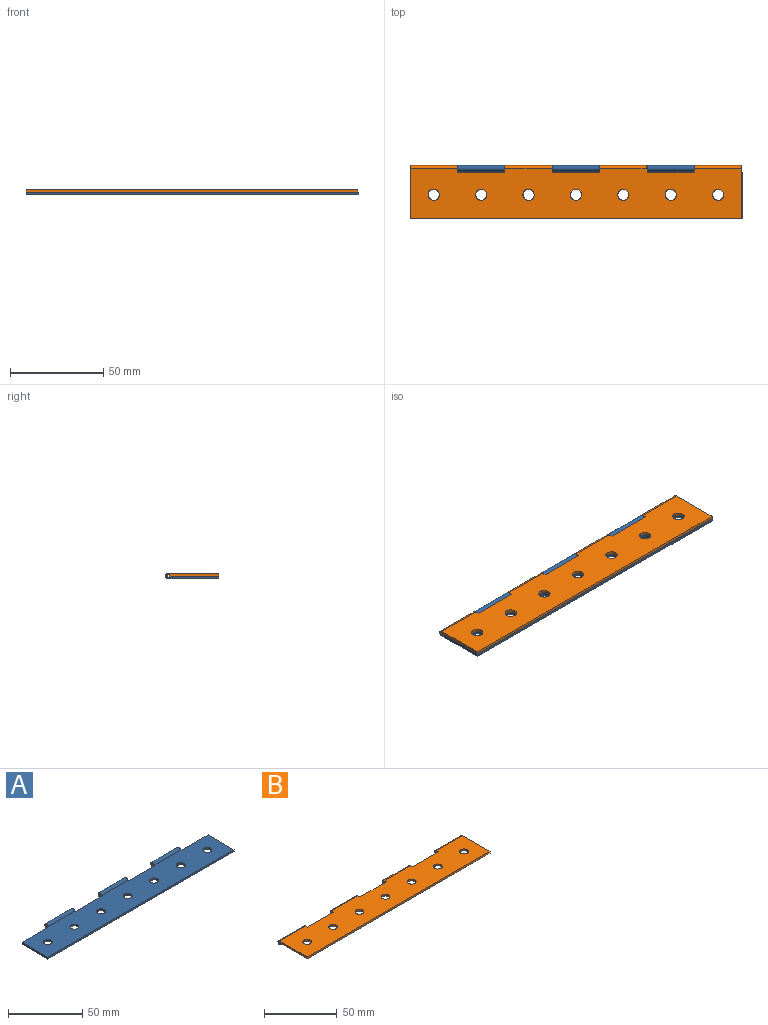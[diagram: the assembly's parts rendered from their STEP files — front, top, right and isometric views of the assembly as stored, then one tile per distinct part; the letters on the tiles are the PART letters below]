
ASSEMBLY  parts=2 mates=1
PART A: 28 faces, bbox 177.8x28.4x3 mm
  f0: plane 177.8x26.9mm, normal (0,0,-1), area 4367.5mm2, adj f1,f2,f3,f5,f6,f7,f8,f9
  f1: cylinder r=1.5mm len=25.28mm, axis (-1,0,0), area 178.5mm2, adj f0,f4,f9,f13
  f2: cylinder r=1.5mm len=25.5mm, axis (-1,0,0), area 180.1mm2, adj f0,f4,f16,f19
  f3: cylinder r=1.5mm len=25.23mm, axis (-1,0,0), area 178.2mm2, adj f0,f4,f12,f17
  f4: plane 177.8x25.4mm, normal (0,0,1), area 4253.6mm2, adj f1,f2,f3,f5,f6,f7,f8,f9
  f5: plane 177.8x1.5mm, normal (0,-1,0), area 266.5mm2, adj f0,f4,f6,f7
  f6: plane 24.77x1.5mm, normal (1,0,0), area 37.1mm2, adj f0,f4,f5,f20
  f7: plane 24.77x1.5mm, normal (-1,0,0), area 37.1mm2, adj f0,f4,f5,f8
  f8: plane 25.45x1.5mm, normal (0,1,0), area 38.1mm2, adj f0,f4,f7,f9
  f9: plane 3.63x3mm, normal (-1,0,0), area 6.7mm2, adj f0,f1,f4,f8,f10
  f10: cylinder r=0.75mm len=25.28mm, axis (-1,0,0), area 119mm2, adj f9,f13
  f11: plane 25.57x1.5mm, normal (0,1,0), area 38.3mm2, adj f0,f4,f12,f13
  f12: plane 3.63x3mm, normal (-1,0,0), area 6.7mm2, adj f0,f3,f4,f11,f14
  f13: plane 3.63x3mm, normal (1,0,0), area 6.7mm2, adj f0,f1,f4,f10,f11
  f14: cylinder r=0.75mm len=25.23mm, axis (-1,0,0), area 118.8mm2, adj f12,f17
  f15: plane 25.17x1.5mm, normal (0,1,0), area 37.7mm2, adj f0,f4,f16,f17
  f16: plane 3.63x3mm, normal (-1,0,0), area 6.7mm2, adj f0,f2,f4,f15,f18
  f17: plane 3.63x3mm, normal (1,0,0), area 6.7mm2, adj f0,f3,f4,f14,f15
  f18: cylinder r=0.75mm len=25.5mm, axis (-1,0,0), area 120.1mm2, adj f16,f19
  f19: plane 3.63x3mm, normal (1,0,0), area 6.7mm2, adj f0,f2,f4,f18,f20
  f20: plane 25.6x1.5mm, normal (0,1,0), area 38.4mm2, adj f0,f4,f6,f19
  f21: cylinder r=3mm len=6mm, axis (0,0,1), area 28.2mm2, adj f0,f4
  f22: cylinder r=3mm len=6mm, axis (0,0,1), area 28.2mm2, adj f0,f4
  f23: cylinder r=3mm len=6mm, axis (0,0,1), area 28.2mm2, adj f0,f4
  f24: cylinder r=3mm len=6mm, axis (0,0,1), area 28.2mm2, adj f0,f4
  f25: cylinder r=3mm len=6mm, axis (0,0,1), area 28.2mm2, adj f0,f4
  f26: cylinder r=3mm len=6mm, axis (0,0,1), area 28.2mm2, adj f0,f4
  f27: cylinder r=3mm len=6mm, axis (0,0,1), area 28.2mm2, adj f0,f4
PART B: 29 faces, bbox 177.8x28.4x3 mm
  f0: cylinder r=1.5mm len=25.4mm, axis (-1,0,0), area 179.5mm2, adj f5,f8,f9,f17
  f1: cylinder r=1.5mm len=25.4mm, axis (-1,0,0), area 179.5mm2, adj f5,f9,f11,f18
  f2: cylinder r=1.5mm len=25.4mm, axis (-1,0,0), area 179.5mm2, adj f5,f9,f12,f14
  f3: cylinder r=1.5mm len=25.4mm, axis (-1,0,0), area 179.5mm2, adj f5,f7,f9,f15
  f4: cylinder r=0.75mm len=25.4mm, axis (-1,0,0), area 119.7mm2, adj f8,f17
  f5: plane 177.8x25.4mm, normal (0,0,-1), area 4279.8mm2, adj f0,f1,f2,f3,f7,f8,f10,f11
  f6: cylinder r=0.75mm len=25.4mm, axis (-1,0,0), area 119.7mm2, adj f7,f15
  f7: plane 28.4x3mm, normal (1,0,0), area 43.9mm2, adj f3,f5,f6,f9,f10
  f8: plane 28.4x3mm, normal (-1,0,0), area 43.9mm2, adj f0,f4,f5,f9,f10
  f9: plane 177.8x26.9mm, normal (0,0,1), area 4432.2mm2, adj f0,f1,f2,f3,f7,f8,f10,f11
  f10: plane 177.8x1.5mm, normal (0,-1,0), area 266.7mm2, adj f5,f7,f8,f9
  f11: plane 3.51x3mm, normal (1,0,0), area 6.5mm2, adj f1,f5,f9,f13,f21
  f12: plane 3.51x3mm, normal (-1,0,0), area 6.5mm2, adj f2,f5,f9,f13,f20
  f13: plane 25.4x1.5mm, normal (0,1,0), area 38.1mm2, adj f5,f9,f11,f12
  f14: plane 3.51x3mm, normal (1,0,0), area 6.5mm2, adj f2,f5,f9,f16,f20
  f15: plane 3.51x3mm, normal (-1,0,0), area 6.5mm2, adj f3,f5,f6,f9,f16
  f16: plane 25.4x1.5mm, normal (0,1,0), area 38.1mm2, adj f5,f9,f14,f15
  f17: plane 3.5x3mm, normal (1,0,0), area 6.5mm2, adj f0,f4,f5,f9,f19
  f18: plane 3.5x3mm, normal (-1,0,0), area 6.5mm2, adj f1,f5,f9,f19,f21
  f19: plane 25.4x1.5mm, normal (0,1,0), area 38.1mm2, adj f5,f9,f17,f18
  f20: cylinder r=0.75mm len=25.4mm, axis (-1,0,0), area 119.7mm2, adj f12,f14
  f21: cylinder r=0.75mm len=25.4mm, axis (-1,0,0), area 119.7mm2, adj f11,f18
  f22: cylinder r=3mm len=6mm, axis (0,0,1), area 28.3mm2, adj f5,f9
  f23: cylinder r=3mm len=6mm, axis (0,0,1), area 28.3mm2, adj f5,f9
  f24: cylinder r=3mm len=6mm, axis (0,0,1), area 28.3mm2, adj f5,f9
  f25: cylinder r=3mm len=6mm, axis (0,0,1), area 28.3mm2, adj f5,f9
  f26: cylinder r=3mm len=6mm, axis (0,0,1), area 28.3mm2, adj f5,f9
  f27: cylinder r=3mm len=6mm, axis (0,0,1), area 28.3mm2, adj f5,f9
  f28: cylinder r=3mm len=6mm, axis (0,0,1), area 28.3mm2, adj f5,f9
PLACE A t=(-1.82,8.13,-5.21)mm
PLACE B t=(-1.89,8.13,-5.21)mm
MATE revolute A.f10 <-> B.f0  axis (1,0,0) through (10.81,8.13,-5.21)mm
